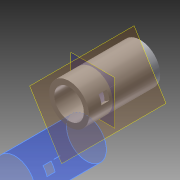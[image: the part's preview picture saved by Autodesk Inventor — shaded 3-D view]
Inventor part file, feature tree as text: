
AUTODESK INVENTOR PART (.ipt)
format: ipt  version: 2013 (Build 170138000, 138)  size: 107,008 bytes
history: native  units: in
note: dims shown in document units (in); Inventor stores cm internally (conversion verified against a paired STEP export)
features: extrude x3, sketch x3, plane x2
ambient origin geometry x8: Origin, YZ Plane, XZ Plane, XY Plane, X Axis, Y Axis, Z Axis, Center Point
bodies: Solid1 (feature_tree)
feature tree (8):
  extrude  "Extrusion1"  Depth=0.84in
  plane  "Work Plane1"
  extrude  "Extrusion3"  [1 undecoded]
  plane  "Work Plane3"
  extrude  "Extrusion4"  Depth=0.25in TaperAngle=0.0deg
  sketch  "Sketch1"  dims[d0=0.622in d2=0.84in]
  sketch  "Sketch3"  dims[d3=1.5in d4=0.0in d7=-1.0in]
  sketch  "Sketch4"  dims[d8=0.125in d9=0.0in d10=0.25in d11=0.0in]
note: 1 required parameter value undecoded (feature->parameter linkage not recoverable at this tier; creation-order binding heuristic only, values carry confidence <= 0.55)
